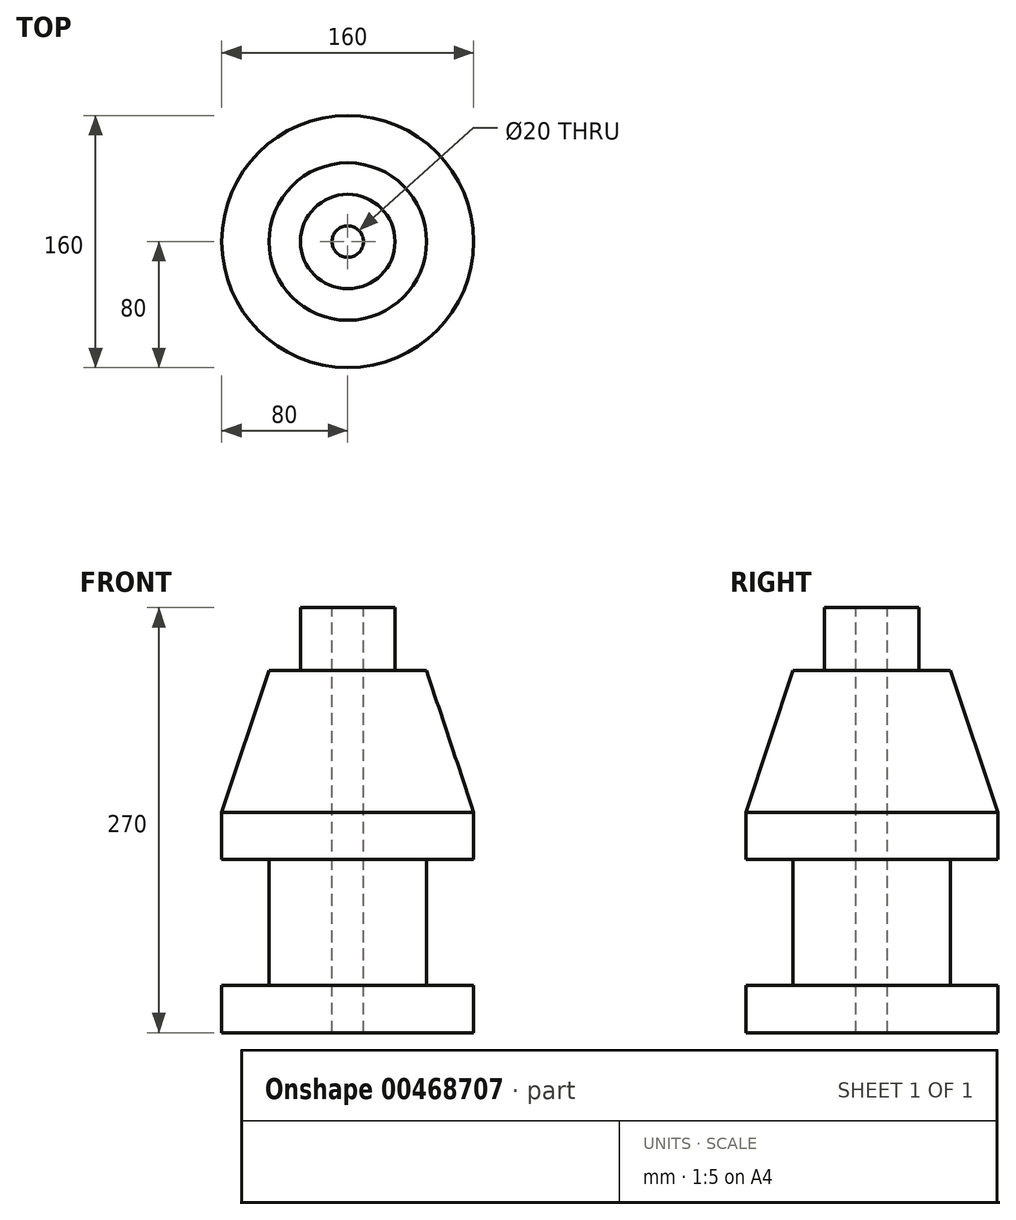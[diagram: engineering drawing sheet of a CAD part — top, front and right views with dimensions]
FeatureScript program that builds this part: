
annotation { "Feature Type Name" : "Feature", "Feature Type Description" : "" }
export const myFeature = defineFeature(function(context is Context, id is Id, definition is map)
    precondition{}
    {
        {
            var Q0;
            Q0=qCreatedBy(makeId("Front.planeOp"),FACE);
            var sketch = newSketch(context, id + "F0", { "sketchPlane" : qUnion([Q0])});
            skLineSegment(sketch, "E0", {"start": v(10, 124.38) * mm, "end": v(10, -145.62) * mm});
            skLineSegment(sketch, "E1", {"start": v(10, 124.38) * mm, "end": v(30, 124.38) * mm});
            skLineSegment(sketch, "E2", {"start": v(30, 124.38) * mm, "end": v(30, 84.38) * mm});
            skLineSegment(sketch, "E3", {"start": v(30, 84.38) * mm, "end": v(50, 84.38) * mm});
            skLineSegment(sketch, "E4", {"start": v(50, 84.38) * mm, "end": v(80, -5.62) * mm});
            skLineSegment(sketch, "E5", {"start": v(80, -5.62) * mm, "end": v(80, -35.62) * mm});
            skLineSegment(sketch, "E6", {"start": v(80, -35.62) * mm, "end": v(50, -35.62) * mm});
            skLineSegment(sketch, "E7", {"start": v(50, -35.62) * mm, "end": v(50, -115.62) * mm});
            skLineSegment(sketch, "E8", {"start": v(50, -115.62) * mm, "end": v(80, -115.62) * mm});
            skLineSegment(sketch, "E9", {"start": v(10, -145.62) * mm, "end": v(80, -145.62) * mm});
            skLineSegment(sketch, "E10", {"start": v(80, -145.62) * mm, "end": v(80, -115.62) * mm});
            skLineSegment(sketch, "E11", {"start": v(0, 145.7) * mm, "end": v(0, -184.88) * mm, "construction": true});
            skSolve(sketch);
        }
        {
            var Q0;
            Q0=makeQuery(id+"F0.imprint","IMPRINT",FACE,{"disambiguationData":[TD([[makeQuery(id+"F0.imprint","IMPRINT",EDGE,{"derivedFrom":sQuery(id+"F0.wireOp",EDGE,"E0")}),1.0]])]});
            var Q1;
            Q1=sQuery(id+"F0.wireOp",EDGE,"E11");
            revolve(context, id + "F1", {"entities" : qUnion([Q0]), "axis" : qUnion([Q1]), "revolveType" : RevolveType.FULL});
        }
    });
